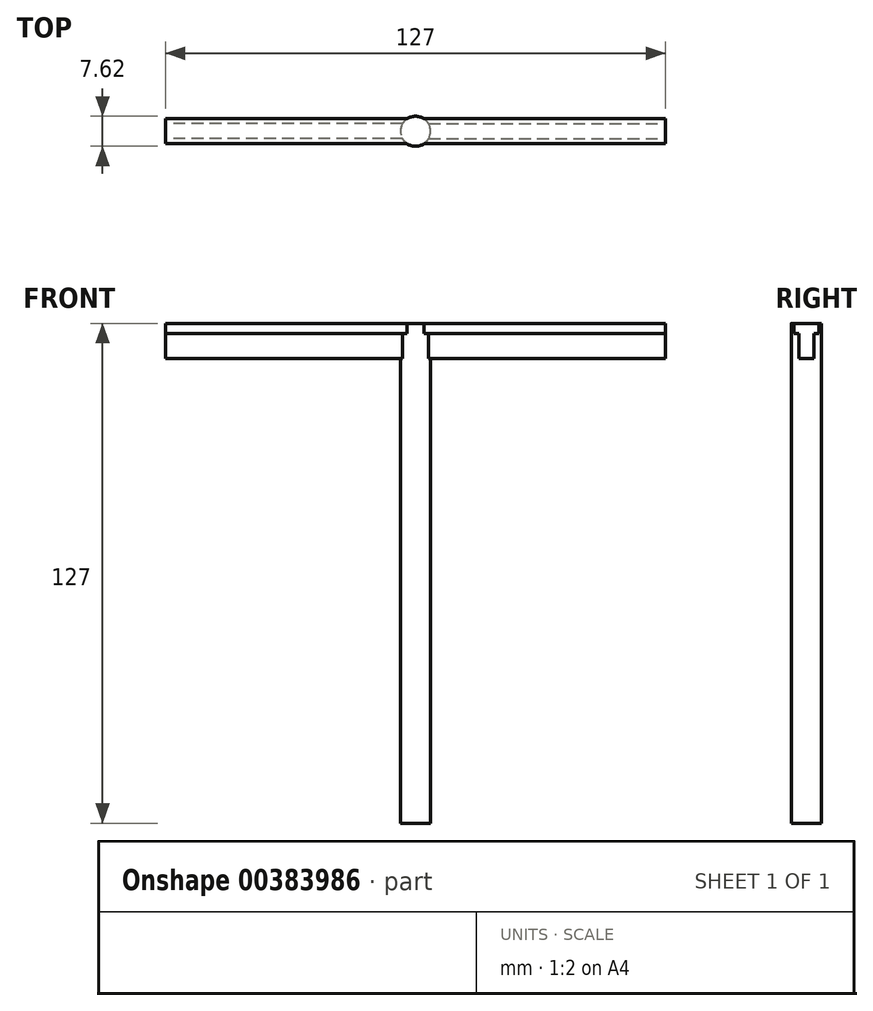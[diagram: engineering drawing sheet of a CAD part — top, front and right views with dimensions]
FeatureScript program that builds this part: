
annotation { "Feature Type Name" : "Feature", "Feature Type Description" : "" }
export const myFeature = defineFeature(function(context is Context, id is Id, definition is map)
    precondition{}
    {
        {
            var Q0;
            Q0=qCreatedBy(makeId("Top.planeOp"),FACE);
            var sketch = newSketch(context, id + "F0", { "sketchPlane" : qUnion([Q0])});
            skCircle(sketch, "E0", {"center": v(0, 0) * mm, "radius": 3.81 * mm});
            skSolve(sketch);
        }
        {
            var Q0;
            Q0=makeQuery(id+"F0.imprint","IMPRINT",FACE,{"disambiguationData":[TD([[makeQuery(id+"F0.imprint","IMPRINT",EDGE,{"derivedFrom":sQuery(id+"F0.wireOp",EDGE,"E0")}),1.0]])]});
            extrude(context, id + "F1", {"entities" : qUnion([Q0]), "depth" : 127 * mm});
        }
        {
            var Q0;
            Q0=makeQuery(id+"F1.opExtrude","CAP_FACE",FACE,{"disambiguationData":[OSD([sQuery(id+"F0.wireOp",EDGE,"E0")])],"isStart":false});
            var sketch = newSketch(context, id + "F2", { "sketchPlane" : qUnion([Q0])});
            skLineSegment(sketch, "E1", {"start": v(0, 3.18) * mm, "end": v(63.5, 3.18) * mm});
            skLineSegment(sketch, "E2", {"start": v(63.5, 3.17) * mm, "end": v(63.5, -3.18) * mm});
            skLineSegment(sketch, "E3", {"start": v(63.5, -3.18) * mm, "end": v(-2.1, -3.18) * mm});
            skLineSegment(sketch, "E4.MirrorCS", {"start": v(-63.5, 3.17) * mm, "end": v(-63.5, -3.18) * mm});
            skLineSegment(sketch, "E5.MirrorCS", {"start": v(0, 3.18) * mm, "end": v(-63.5, 3.17) * mm});
            skLineSegment(sketch, "E6.MirrorCS", {"start": v(-63.5, -3.18) * mm, "end": v(2.1, -3.18) * mm});
            skSolve(sketch);
        }
        {
            var Q0;
            {var subQ0=sQuery(id+"F2.wireOp",EDGE,"E1");Q0=makeQuery(id+"F2.imprint","IMPRINT",FACE,{"disambiguationData":[TD([[makeQuery(id+"F2.imprint","IMPRINT",EDGE,{"derivedFrom":subQ0}),-1.0]])]});}
            var Q1;
            Q1=makeQuery(id+"F2.imprint","IMPRINT",FACE,{"disambiguationData":[TD([[makeQuery(id+"F2.imprint","IMPRINT",EDGE,{"derivedFrom":sQuery(id+"F2.wireOp",EDGE,"E4.MirrorCS")}),1.0]])]});
            extrude(context, id + "F3", {"entities" : qUnion([Q0, Q1]), "operationType" : NewBodyOperationType.ADD, "oppositeDirection" : true, "depth" : 8.9 * mm});
        }
        {
            var Q0;
            Q0=makeQuery(id+"F3.opExtrude","SWEPT_FACE",FACE,{"disambiguationData":[OSD([sQuery(id+"F2.wireOp",EDGE,"E2")])]});
            var sketch = newSketch(context, id + "F4", { "sketchPlane" : qUnion([Q0])});
            skLineSegment(sketch, "E7.bottom", {"start": v(-3.18, 118.11) * mm, "end": v(-1.9, 118.11) * mm});
            skLineSegment(sketch, "E7.top", {"start": v(-3.18, 124.46) * mm, "end": v(-1.9, 124.46) * mm});
            skLineSegment(sketch, "E7.left", {"start": v(-3.18, 118.11) * mm, "end": v(-3.18, 124.46) * mm});
            skLineSegment(sketch, "E7.right", {"start": v(-1.9, 118.11) * mm, "end": v(-1.9, 124.46) * mm});
            skLineSegment(sketch, "E8.bottom", {"start": v(3.18, 118.11) * mm, "end": v(1.9, 118.11) * mm});
            skLineSegment(sketch, "E8.top", {"start": v(3.18, 124.46) * mm, "end": v(1.9, 124.46) * mm});
            skLineSegment(sketch, "E8.left", {"start": v(3.18, 118.11) * mm, "end": v(3.18, 124.46) * mm});
            skLineSegment(sketch, "E8.right", {"start": v(1.9, 118.11) * mm, "end": v(1.9, 124.46) * mm});
            skSolve(sketch);
        }
        {
            var Q0;
            Q0=makeQuery(id+"F4.imprint","IMPRINT",FACE,{"disambiguationData":[TD([[makeQuery(id+"F4.imprint","IMPRINT",EDGE,{"derivedFrom":sQuery(id+"F4.wireOp",EDGE,"E7.bottom")}),-1.0]])]});
            var Q1;
            Q1=makeQuery(id+"F4.imprint","IMPRINT",FACE,{"disambiguationData":[TD([[makeQuery(id+"F4.imprint","IMPRINT",EDGE,{"derivedFrom":sQuery(id+"F4.wireOp",EDGE,"E8.bottom")}),-1.0]])]});
            var Q2;
            Q2=makeQuery(id+"F1.opExtrude","SWEPT_FACE",FACE,{"disambiguationData":[OSD([sQuery(id+"F0.wireOp",EDGE,"E0")])]});
            extrude(context, id + "F5", {"entities" : qUnion([Q0, Q1]), "operationType" : NewBodyOperationType.REMOVE, "endBound" : BoundingType.UP_TO_SURFACE, "oppositeDirection" : true, "endBoundEntityFace" : qUnion([Q2]), "depth" : 25.4 * mm});
        }
        {
            var Q0;
            Q0=makeQuery(id+"F3.opExtrude","SWEPT_FACE",FACE,{"disambiguationData":[OSD([sQuery(id+"F2.wireOp",EDGE,"E4.MirrorCS")])]});
            var sketch = newSketch(context, id + "F6", { "sketchPlane" : qUnion([Q0])});
            skLineSegment(sketch, "E9.bottom", {"start": v(-3.17, 118.11) * mm, "end": v(-1.9, 118.11) * mm});
            skLineSegment(sketch, "E9.top", {"start": v(-3.17, 124.46) * mm, "end": v(-1.9, 124.46) * mm});
            skLineSegment(sketch, "E9.left", {"start": v(-3.17, 118.11) * mm, "end": v(-3.17, 124.46) * mm});
            skLineSegment(sketch, "E9.right", {"start": v(-1.9, 118.11) * mm, "end": v(-1.9, 124.46) * mm});
            skLineSegment(sketch, "E10.bottom", {"start": v(3.18, 118.11) * mm, "end": v(1.9, 118.11) * mm});
            skLineSegment(sketch, "E10.top", {"start": v(3.18, 124.46) * mm, "end": v(1.9, 124.46) * mm});
            skLineSegment(sketch, "E10.left", {"start": v(3.18, 118.11) * mm, "end": v(3.18, 124.46) * mm});
            skLineSegment(sketch, "E10.right", {"start": v(1.9, 118.11) * mm, "end": v(1.9, 124.46) * mm});
            skSolve(sketch);
        }
        {
            var Q0;
            Q0=makeQuery(id+"F6.imprint","IMPRINT",FACE,{"disambiguationData":[TD([[makeQuery(id+"F6.imprint","IMPRINT",EDGE,{"derivedFrom":sQuery(id+"F6.wireOp",EDGE,"E9.bottom")}),1.0]])]});
            var Q1;
            Q1=makeQuery(id+"F6.imprint","IMPRINT",FACE,{"disambiguationData":[TD([[makeQuery(id+"F6.imprint","IMPRINT",EDGE,{"derivedFrom":sQuery(id+"F6.wireOp",EDGE,"E10.bottom")}),1.0]])]});
            var Q2;
            {var subQ0=sQuery(id+"F0.wireOp",EDGE,"E0");Q2=makeQuery(id+"F5.boolean.opBoolean","MERGE",FACE,{"derivedFrom":[makeQuery(id+"F1.opExtrude","SWEPT_FACE",FACE,{"disambiguationData":[OSD([subQ0])]}),makeQuery(id+"F5.opExtrude","CAP_FACE",FACE,{"disambiguationData":[OSD([subQ0]),ownerDisambiguation([makeQuery(id+"F4.imprint","IMPRINT",EDGE,{"derivedFrom":sQuery(id+"F4.wireOp",EDGE,"E7.bottom")})])],"isStart":false}),makeQuery(id+"F5.opExtrude","CAP_FACE",FACE,{"disambiguationData":[OSD([subQ0]),ownerDisambiguation([makeQuery(id+"F4.imprint","IMPRINT",EDGE,{"derivedFrom":sQuery(id+"F4.wireOp",EDGE,"E8.bottom")})])],"isStart":false})]});}
            extrude(context, id + "F7", {"entities" : qUnion([Q0, Q1]), "operationType" : NewBodyOperationType.REMOVE, "endBound" : BoundingType.UP_TO_SURFACE, "oppositeDirection" : true, "endBoundEntityFace" : qUnion([Q2]), "depth" : 25.4 * mm});
        }
    });
